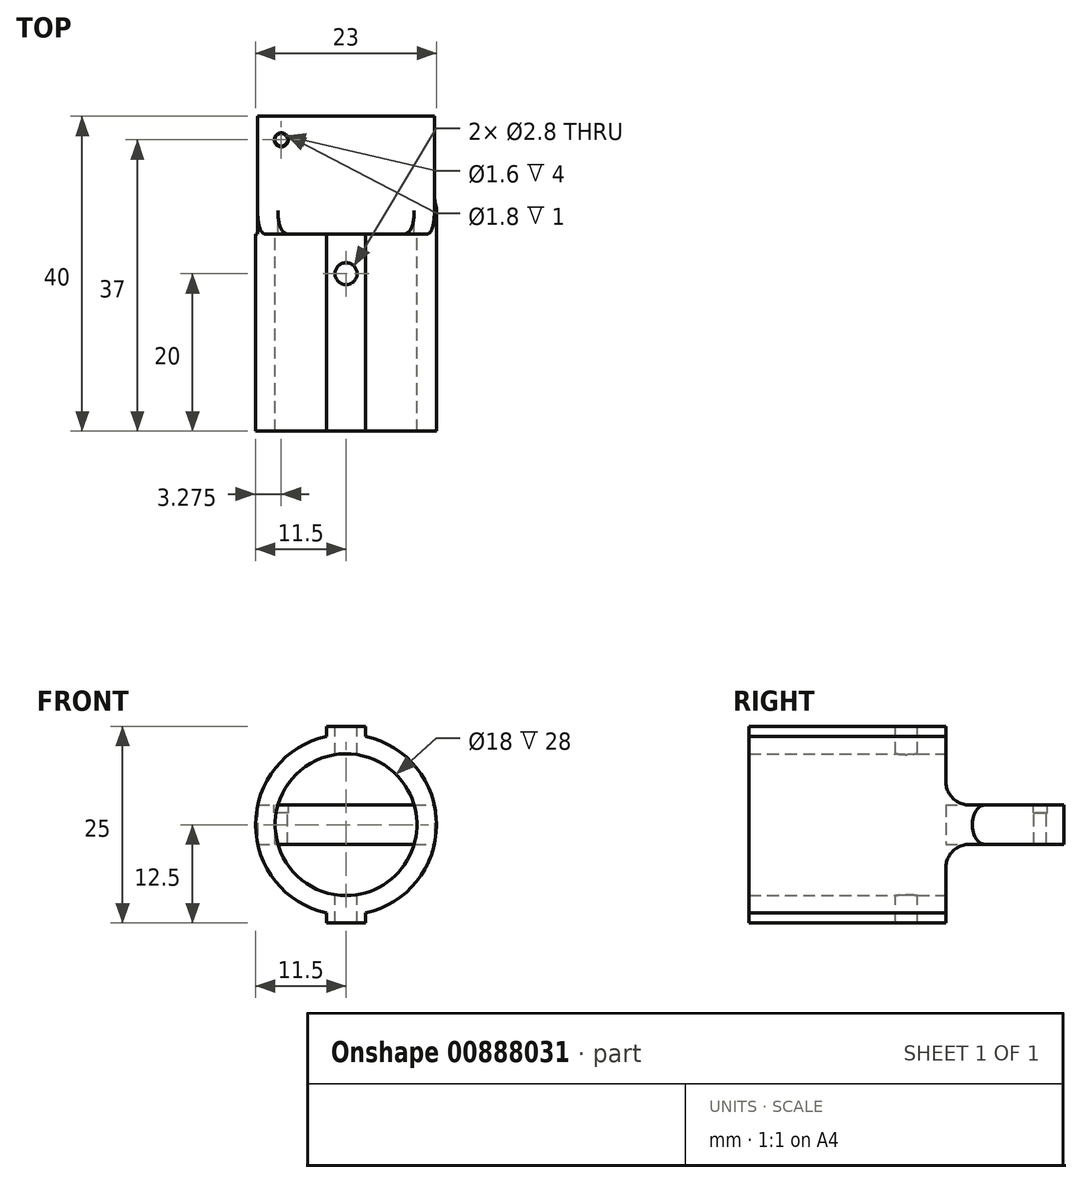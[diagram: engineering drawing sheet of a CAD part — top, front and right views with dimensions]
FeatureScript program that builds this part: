
annotation { "Feature Type Name" : "Feature", "Feature Type Description" : "" }
export const myFeature = defineFeature(function(context is Context, id is Id, definition is map)
    precondition{}
    {
        {
            var Q0;
            Q0=qCreatedBy(makeId("Front.planeOp"),FACE);
            var sketch = newSketch(context, id + "F0", { "sketchPlane" : qUnion([Q0])});
            skCircle(sketch, "E0", {"center": v(0, 0) * mm, "radius": 9 * mm});
            skCircle(sketch, "E1", {"center": v(0, 0) * mm, "radius": 11.5 * mm});
            skLineSegment(sketch, "E2.bottom", {"start": v(-2.5, 12.5) * mm, "end": v(2.5, 12.5) * mm});
            skLineSegment(sketch, "E2.top", {"start": v(-2.5, -12.5) * mm, "end": v(2.5, -12.5) * mm});
            skLineSegment(sketch, "E2.left", {"start": v(-2.5, 12.5) * mm, "end": v(-2.5, -12.5) * mm});
            skLineSegment(sketch, "E2.right", {"start": v(2.5, 12.5) * mm, "end": v(2.5, -12.5) * mm});
            skSolve(sketch);
        }
        {
            var Q0;
            Q0=qSketchRegion(id+"F0",true);
            extrude(context, id + "F1", {"entities" : qUnion([Q0]), "depth" : 25 * mm, "offsetDistance" : 25 * mm});
        }
        {
            var Q0;
            Q0=makeQuery(id+"F1.opExtrude","CAP_FACE",FACE,{"disambiguationData":[OSD([sQuery(id+"F0.wireOp",EDGE,"E0"),sQuery(id+"F0.wireOp",EDGE,"E1")])],"isStart":true});
            var sketch = newSketch(context, id + "F2", { "sketchPlane" : qUnion([Q0])});
            skLineSegment(sketch, "E3.bottom", {"start": v(11.22, 2.5) * mm, "end": v(-11.22, 2.5) * mm});
            skLineSegment(sketch, "E3.top", {"start": v(11.22, -2.5) * mm, "end": v(-11.22, -2.5) * mm});
            skLineSegment(sketch, "E3.left", {"start": v(11.22, 2.5) * mm, "end": v(11.22, -2.5) * mm});
            skLineSegment(sketch, "E3.right", {"start": v(-11.22, 2.5) * mm, "end": v(-11.22, -2.5) * mm});
            skPoint(sketch, "E3.middle", {"position": v(0, 0) * mm});
            skSolve(sketch);
        }
        {
            var Q0;
            Q0=qSketchRegion(id+"F2",true);
            extrude(context, id + "F3", {"entities" : qUnion([Q0]), "operationType" : NewBodyOperationType.ADD, "depth" : 15 * mm, "offsetDistance" : 25 * mm});
        }
        {
            var Q0;
            Q0=makeQuery(id+"F3.opExtrude","SWEPT_FACE",FACE,{"disambiguationData":[OSD([sQuery(id+"F2.wireOp",EDGE,"E3.bottom")])]});
            var sketch = newSketch(context, id + "F4", { "sketchPlane" : qUnion([Q0])});
            skCircle(sketch, "E4", {"center": v(-8.22, 12) * mm, "radius": 0.8 * mm});
            skSolve(sketch);
        }
        {
            var Q0;
            Q0=qSketchRegion(id+"F4",true);
            extrude(context, id + "F5", {"entities" : qUnion([Q0]), "operationType" : NewBodyOperationType.REMOVE, "oppositeDirection" : true, "depth" : 25 * mm, "offsetDistance" : 25 * mm});
        }
        {
            var Q0;
            Q0=makeQuery(id+"F1.opExtrude","SWEPT_FACE",FACE,{"disambiguationData":[OSD([sQuery(id+"F0.wireOp",EDGE,"E2.bottom")])]});
            var sketch = newSketch(context, id + "F6", { "sketchPlane" : qUnion([Q0])});
            skCircle(sketch, "E5", {"center": v(0, -5) * mm, "radius": 1.4 * mm});
            skSolve(sketch);
        }
        {
            var Q0;
            Q0=qSketchRegion(id+"F6",true);
            extrude(context, id + "F7", {"entities" : qUnion([Q0]), "operationType" : NewBodyOperationType.REMOVE, "oppositeDirection" : true, "depth" : 25 * mm, "offsetDistance" : 25 * mm});
        }
        {
            var Q0;
            Q0=makeQuery(id+"F3.opExtrude","SWEPT_FACE",FACE,{"disambiguationData":[OSD([sQuery(id+"F2.wireOp",EDGE,"E3.bottom")])]});
            var sketch = newSketch(context, id + "F8", { "sketchPlane" : qUnion([Q0])});
            skCircle(sketch, "E6", {"center": v(-8.22, 12) * mm, "radius": 0.9 * mm});
            skSolve(sketch);
        }
        {
            var Q0;
            Q0=qSketchRegion(id+"F8",true);
            extrude(context, id + "F9", {"entities" : qUnion([Q0]), "operationType" : NewBodyOperationType.REMOVE, "oppositeDirection" : true, "depth" : 1 * mm, "offsetDistance" : 25 * mm});
        }
        {
            var Q0;
            {var subQ0=sQuery(id+"F2.wireOp",EDGE,"E3.left");var subQ1=sQuery(id+"F2.wireOp",EDGE,"E3.top");var subQ2=sQuery(id+"F0.wireOp",EDGE,"E2.left");var subQ3=sQuery(id+"F0.wireOp",EDGE,"E1");var subQ4=sQuery(id+"F0.wireOp",EDGE,"E0");var subQ5=makeQuery(id+"F1.opExtrude","CAP_FACE",FACE,{"disambiguationData":[OSD([subQ4,subQ3,sQuery(id+"F0.wireOp",EDGE,"E2.bottom"),sQuery(id+"F0.wireOp",EDGE,"E2.top"),subQ2,sQuery(id+"F0.wireOp",EDGE,"E2.right")])],"isStart":true});var subQ6=makeQuery(id+"F3.opExtrude","SWEPT_FACE",FACE,{"disambiguationData":[OSD([subQ1])]});Q0=makeQuery(id+"F3.boolean.opBoolean","SPLIT",EDGE,{"disambiguationData":[topologyDisambiguationEdgeConnected([subQ5,subQ6]),TD([makeQuery(id+"F3.opExtrude","SWEPT_FACE",FACE,{"disambiguationData":[OSD([subQ0])]})])],"derivedFrom":makeQuery(id+"F3.opExtrude","CAP_EDGE",EDGE,{"disambiguationData":[OSD([subQ1])],"isStart":true})});}
            var Q1;
            {var subQ0=sQuery(id+"F2.wireOp",EDGE,"E3.right");var subQ1=sQuery(id+"F2.wireOp",EDGE,"E3.top");var subQ2=sQuery(id+"F0.wireOp",EDGE,"E2.right");var subQ3=sQuery(id+"F0.wireOp",EDGE,"E1");var subQ4=makeQuery(id+"F3.opExtrude","SWEPT_FACE",FACE,{"disambiguationData":[OSD([subQ1])]});var subQ5=sQuery(id+"F0.wireOp",EDGE,"E0");var subQ6=makeQuery(id+"F1.opExtrude","CAP_FACE",FACE,{"disambiguationData":[OSD([subQ5,subQ3,sQuery(id+"F0.wireOp",EDGE,"E2.bottom"),sQuery(id+"F0.wireOp",EDGE,"E2.top"),sQuery(id+"F0.wireOp",EDGE,"E2.left"),subQ2])],"isStart":true});Q1=makeQuery(id+"F3.boolean.opBoolean","SPLIT",EDGE,{"disambiguationData":[topologyDisambiguationEdgeConnected([subQ6,subQ4]),TD([makeQuery(id+"F3.opExtrude","SWEPT_FACE",FACE,{"disambiguationData":[OSD([subQ0])]})])],"derivedFrom":makeQuery(id+"F3.opExtrude","CAP_EDGE",EDGE,{"disambiguationData":[OSD([subQ1])],"isStart":true})});}
            var Q2;
            {var subQ0=sQuery(id+"F2.wireOp",EDGE,"E3.bottom");var subQ1=makeQuery(id+"F3.opExtrude","SWEPT_FACE",FACE,{"disambiguationData":[OSD([subQ0])]});var subQ2=sQuery(id+"F0.wireOp",EDGE,"E2.right");var subQ3=sQuery(id+"F0.wireOp",EDGE,"E1");var subQ4=sQuery(id+"F0.wireOp",EDGE,"E0");var subQ5=makeQuery(id+"F1.opExtrude","CAP_FACE",FACE,{"disambiguationData":[OSD([subQ4,subQ3,sQuery(id+"F0.wireOp",EDGE,"E2.bottom"),sQuery(id+"F0.wireOp",EDGE,"E2.top"),sQuery(id+"F0.wireOp",EDGE,"E2.left"),subQ2])],"isStart":true});var subQ6=sQuery(id+"F2.wireOp",EDGE,"E3.right");Q2=makeQuery(id+"F3.boolean.opBoolean","SPLIT",EDGE,{"disambiguationData":[topologyDisambiguationEdgeConnected([subQ5,subQ1]),TD([makeQuery(id+"F3.opExtrude","SWEPT_FACE",FACE,{"disambiguationData":[OSD([subQ6])]})])],"derivedFrom":makeQuery(id+"F3.opExtrude","CAP_EDGE",EDGE,{"disambiguationData":[OSD([subQ0])],"isStart":true})});}
            var Q3;
            {var subQ0=sQuery(id+"F2.wireOp",EDGE,"E3.bottom");var subQ1=makeQuery(id+"F3.opExtrude","SWEPT_FACE",FACE,{"disambiguationData":[OSD([subQ0])]});var subQ2=sQuery(id+"F0.wireOp",EDGE,"E2.left");var subQ3=sQuery(id+"F0.wireOp",EDGE,"E1");var subQ4=sQuery(id+"F0.wireOp",EDGE,"E0");var subQ5=makeQuery(id+"F1.opExtrude","CAP_FACE",FACE,{"disambiguationData":[OSD([subQ4,subQ3,sQuery(id+"F0.wireOp",EDGE,"E2.bottom"),sQuery(id+"F0.wireOp",EDGE,"E2.top"),subQ2,sQuery(id+"F0.wireOp",EDGE,"E2.right")])],"isStart":true});var subQ6=sQuery(id+"F2.wireOp",EDGE,"E3.left");Q3=makeQuery(id+"F3.boolean.opBoolean","SPLIT",EDGE,{"disambiguationData":[topologyDisambiguationEdgeConnected([subQ5,subQ1]),TD([makeQuery(id+"F3.opExtrude","SWEPT_FACE",FACE,{"disambiguationData":[OSD([subQ6])]})])],"derivedFrom":makeQuery(id+"F3.opExtrude","CAP_EDGE",EDGE,{"disambiguationData":[OSD([subQ0])],"isStart":true})});}
            fillet(context, id + "F10", {"entities" : qUnion([Q0, Q1, Q2, Q3]), "radius" : 3 * mm, "tangentPropagation" : true, "allowEdgeOverflow" : false});
        }
        {
            var Q0;
            Q0=makeQuery(id+"F3.opExtrude","CAP_EDGE",EDGE,{"disambiguationData":[OSD([sQuery(id+"F2.wireOp",EDGE,"E3.right")])],"isStart":true});
            var Q1;
            Q1=makeQuery(id+"F3.opExtrude","CAP_EDGE",EDGE,{"disambiguationData":[OSD([sQuery(id+"F2.wireOp",EDGE,"E3.left")])],"isStart":true});
            fillet(context, id + "F11", {"entities" : qUnion([Q0, Q1]), "radius" : 5 * mm, "tangentPropagation" : true, "allowEdgeOverflow" : false});
        }
    });
